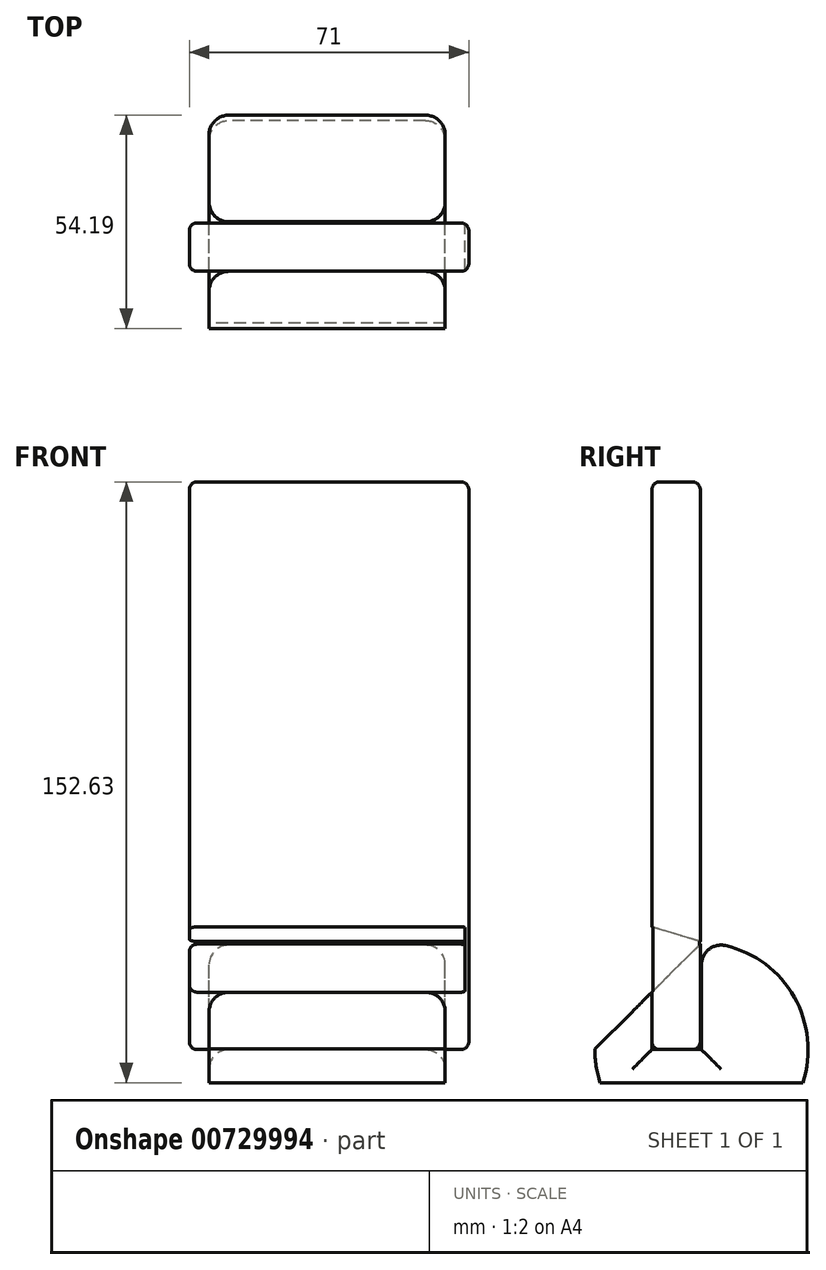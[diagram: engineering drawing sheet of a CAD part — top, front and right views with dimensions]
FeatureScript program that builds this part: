
annotation { "Feature Type Name" : "Feature", "Feature Type Description" : "" }
export const myFeature = defineFeature(function(context is Context, id is Id, definition is map)
    precondition{}
    {
        {
            var Q0;
            Q0=qCreatedBy(makeId("Right.planeOp"),FACE);
            var sketch = newSketch(context, id + "F0", { "sketchPlane" : qUnion([Q0])});
            skLineSegment(sketch, "E0.bottom", {"start": v(0, 0) * mm, "end": v(12.3, 0) * mm});
            skLineSegment(sketch, "E0.top", {"start": v(0, 144.2) * mm, "end": v(12.3, 144.2) * mm});
            skLineSegment(sketch, "E0.left", {"start": v(0, 0) * mm, "end": v(0, 144.2) * mm});
            skLineSegment(sketch, "E0.right", {"start": v(12.3, 0) * mm, "end": v(12.3, 144.2) * mm});
            skSolve(sketch);
        }
        {
            var Q0;
            Q0=makeQuery(id+"F0.imprint","IMPRINT",FACE,{"disambiguationData":[TD([[makeQuery(id+"F0.imprint","IMPRINT",EDGE,{"derivedFrom":sQuery(id+"F0.wireOp",EDGE,"E0.bottom")}),1.0]])]});
            extrude(context, id + "F1", {"entities" : qUnion([Q0]), "depth" : 71 * mm, "offsetDistance" : 25 * mm});
        }
        {
            var Q0;
            Q0=makeQuery(id+"F1.opExtrude","SWEPT_EDGE",EDGE,{"disambiguationData":[OSD([sQuery(id+"F0.wireOp",EDGE,"E0.top"),sQuery(id+"F0.wireOp",EDGE,"E0.right")])]});
            var Q1;
            Q1=makeQuery(id+"F1.opExtrude","CAP_FACE",FACE,{"disambiguationData":[OSD([sQuery(id+"F0.wireOp",EDGE,"E0.bottom"),sQuery(id+"F0.wireOp",EDGE,"E0.top"),sQuery(id+"F0.wireOp",EDGE,"E0.left"),sQuery(id+"F0.wireOp",EDGE,"E0.right")])],"isStart":true});
            var Q2;
            Q2=makeQuery(id+"F1.opExtrude","SWEPT_EDGE",EDGE,{"disambiguationData":[OSD([sQuery(id+"F0.wireOp",EDGE,"E0.bottom"),sQuery(id+"F0.wireOp",EDGE,"E0.right")])]});
            var Q3;
            Q3=makeQuery(id+"F1.opExtrude","CAP_FACE",FACE,{"disambiguationData":[OSD([sQuery(id+"F0.wireOp",EDGE,"E0.bottom"),sQuery(id+"F0.wireOp",EDGE,"E0.top"),sQuery(id+"F0.wireOp",EDGE,"E0.left"),sQuery(id+"F0.wireOp",EDGE,"E0.right")])],"isStart":false});
            var Q4;
            Q4=makeQuery(id+"F1.opExtrude","SWEPT_FACE",FACE,{"disambiguationData":[OSD([sQuery(id+"F0.wireOp",EDGE,"E0.top")])]});
            var Q5;
            Q5=makeQuery(id+"F1.opExtrude","SWEPT_FACE",FACE,{"disambiguationData":[OSD([sQuery(id+"F0.wireOp",EDGE,"E0.left")])]});
            var Q6;
            Q6=makeQuery(id+"F1.opExtrude","SWEPT_FACE",FACE,{"disambiguationData":[OSD([sQuery(id+"F0.wireOp",EDGE,"E0.right")])]});
            var Q7;
            Q7=makeQuery(id+"F1.opExtrude","SWEPT_FACE",FACE,{"disambiguationData":[OSD([sQuery(id+"F0.wireOp",EDGE,"E0.bottom")])]});
            var Q8;
            Q8=makeQuery(id+"F1.opExtrude","SWEPT_EDGE",EDGE,{"disambiguationData":[OSD([sQuery(id+"F0.wireOp",EDGE,"E0.top"),sQuery(id+"F0.wireOp",EDGE,"E0.left")])]});
            var Q9;
            Q9=makeQuery(id+"F1.opExtrude","CAP_EDGE",EDGE,{"disambiguationData":[OSD([sQuery(id+"F0.wireOp",EDGE,"E0.bottom")])],"isStart":true});
            var Q10;
            Q10=makeQuery(id+"F1.opExtrude","CAP_EDGE",EDGE,{"disambiguationData":[OSD([sQuery(id+"F0.wireOp",EDGE,"E0.bottom")])],"isStart":false});
            var Q11;
            Q11=makeQuery(id+"F1.opExtrude","CAP_EDGE",EDGE,{"disambiguationData":[OSD([sQuery(id+"F0.wireOp",EDGE,"E0.top")])],"isStart":true});
            var Q12;
            Q12=makeQuery(id+"F1.opExtrude","CAP_EDGE",EDGE,{"disambiguationData":[OSD([sQuery(id+"F0.wireOp",EDGE,"E0.left")])],"isStart":false});
            var Q13;
            Q13=makeQuery(id+"F1.opExtrude","CAP_EDGE",EDGE,{"disambiguationData":[OSD([sQuery(id+"F0.wireOp",EDGE,"E0.left")])],"isStart":true});
            var Q14;
            Q14=makeQuery(id+"F1.opExtrude","CAP_EDGE",EDGE,{"disambiguationData":[OSD([sQuery(id+"F0.wireOp",EDGE,"E0.right")])],"isStart":false});
            var Q15;
            Q15=makeQuery(id+"F1.opExtrude","CAP_EDGE",EDGE,{"disambiguationData":[OSD([sQuery(id+"F0.wireOp",EDGE,"E0.right")])],"isStart":true});
            var Q16;
            Q16=makeQuery(id+"F1.opExtrude","SWEPT_EDGE",EDGE,{"disambiguationData":[OSD([sQuery(id+"F0.wireOp",EDGE,"E0.bottom"),sQuery(id+"F0.wireOp",EDGE,"E0.left")])]});
            var Q17;
            Q17=makeQuery(id+"F1.opExtrude","CAP_EDGE",EDGE,{"disambiguationData":[OSD([sQuery(id+"F0.wireOp",EDGE,"E0.top")])],"isStart":false});
            fillet(context, id + "F2", {"entities" : qUnion([Q0, Q1, Q2, Q3, Q4, Q5, Q6, Q7, Q8, Q9, Q10, Q11, Q12, Q13, Q14, Q15, Q16, Q17]), "radius" : 2 * mm, "tangentPropagation" : true, "allowEdgeOverflow" : false});
        }
        {
            var Q0;
            Q0=makeQuery(id+"F1.opExtrude","SWEPT_BODY",BODY,{"disambiguationData":[OSD([sQuery(id+"F0.wireOp",EDGE,"E0.bottom"),sQuery(id+"F0.wireOp",EDGE,"E0.top"),sQuery(id+"F0.wireOp",EDGE,"E0.left"),sQuery(id+"F0.wireOp",EDGE,"E0.right")])]});
            var Q1;
            Q1=qCreatedBy(makeId("Origin.pointOp"),VERTEX);
            transform(context, id + "F3", {"entities" : qUnion([Q0]), "transformType" : TransformType.TRANSLATION_3D, "dx" : -35 * mm, "dy" : 0 * mm, "dz" : 0 * mm, "makeCopy" : false});
        }
        {
            var Q0;
            Q0=qCreatedBy(makeId("Right.planeOp"),FACE);
            var sketch = newSketch(context, id + "F4", { "sketchPlane" : qUnion([Q0])});
            skLineSegment(sketch, "E1.bottom", {"start": v(0, 0) * mm, "end": v(12.58, 0) * mm});
            skLineSegment(sketch, "E1.top", {"start": v(0, 49.2) * mm, "end": v(12.58, 49.2) * mm});
            skLineSegment(sketch, "E1.left", {"start": v(0, 0) * mm, "end": v(0, 49.2) * mm});
            skLineSegment(sketch, "E1.right", {"start": v(12.58, 0) * mm, "end": v(12.58, 49.2) * mm});
            skCircle(sketch, "E2", {"center": v(12.58, 0) * mm, "radius": 27.1 * mm});
            skLineSegment(sketch, "E3.bottom", {"start": v(-28.1, 38.83) * mm, "end": v(49.11, 38.83) * mm});
            skLineSegment(sketch, "E3.top", {"start": v(-28.1, -8.43) * mm, "end": v(49.11, -8.43) * mm});
            skLineSegment(sketch, "E3.left", {"start": v(-28.1, 38.83) * mm, "end": v(-28.1, -8.43) * mm});
            skLineSegment(sketch, "E3.right", {"start": v(49.11, 38.83) * mm, "end": v(49.11, -8.43) * mm});
            skSolve(sketch);
        }
        {
            var Q0;
            {var subQ5=sQuery(id+"F4.wireOp",EDGE,"E1.bottom");Q0=makeQuery(id+"F4.imprint","IMPRINT",FACE,{"disambiguationData":[TD([[makeQuery(id+"F4.imprint","IMPRINT",EDGE,{"derivedFrom":subQ5}),-1.0]])]});}
            extrude(context, id + "F5", {"entities" : qUnion([Q0]), "depth" : 60 * mm, "offsetDistance" : 25 * mm});
        }
        {
            var Q0;
            Q0=makeQuery(id+"F5.opExtrude","SWEPT_BODY",BODY,{"disambiguationData":[OSD([sQuery(id+"F4.wireOp",EDGE,"E1.bottom"),sQuery(id+"F4.wireOp",EDGE,"E1.left"),sQuery(id+"F4.wireOp",EDGE,"E1.right"),sQuery(id+"F4.wireOp",EDGE,"E2"),sQuery(id+"F4.wireOp",EDGE,"E3.top")])]});
            transform(context, id + "F6", {"entities" : qUnion([Q0]), "transformType" : TransformType.TRANSLATION_3D, "dx" : -30 * mm, "dy" : 0 * mm, "dz" : 0 * mm, "makeCopy" : false});
        }
        {
            var Q0;
            Q0=qCreatedBy(makeId("Right.planeOp"),FACE);
            var sketch = newSketch(context, id + "F7", { "sketchPlane" : qUnion([Q0])});
            skLineSegment(sketch, "E4", {"start": v(-14.65, 0) * mm, "end": v(12.82, 27.28) * mm});
            skLineSegment(sketch, "E5", {"start": v(12.82, 27.28) * mm, "end": v(-8.53, 33.7) * mm});
            skLineSegment(sketch, "E6", {"start": v(-8.53, 33.7) * mm, "end": v(-30.89, 16.46) * mm});
            skLineSegment(sketch, "E7", {"start": v(-30.89, 16.46) * mm, "end": v(-14.65, 0) * mm});
            skSolve(sketch);
        }
        {
            var Q0;
            Q0=makeQuery(id+"F7.imprint","IMPRINT",FACE,{"disambiguationData":[TD([[makeQuery(id+"F7.imprint","IMPRINT",EDGE,{"derivedFrom":sQuery(id+"F7.wireOp",EDGE,"E4")}),1.0]])]});
            extrude(context, id + "F8", {"entities" : qUnion([Q0]), "operationType" : NewBodyOperationType.REMOVE, "endBound" : BoundingType.SYMMETRIC, "oppositeDirection" : true, "depth" : 70 * mm, "offsetDistance" : 25 * mm});
        }
        {
            var Q0;
            Q0=makeQuery(id+"F5.opExtrude","CAP_EDGE",EDGE,{"disambiguationData":[OSD([sQuery(id+"F4.wireOp",EDGE,"E1.right")])],"isStart":false});
            var Q1;
            Q1=makeQuery(id+"F5.opExtrude","CAP_EDGE",EDGE,{"disambiguationData":[OSD([sQuery(id+"F4.wireOp",EDGE,"E1.bottom")])],"isStart":false});
            var Q2;
            Q2=makeQuery(id+"F5.opExtrude","CAP_EDGE",EDGE,{"disambiguationData":[OSD([sQuery(id+"F4.wireOp",EDGE,"E1.bottom")])],"isStart":true});
            var Q3;
            Q3=makeQuery(id+"F5.opExtrude","CAP_EDGE",EDGE,{"disambiguationData":[OSD([sQuery(id+"F4.wireOp",EDGE,"E1.left")])],"isStart":true});
            var Q4;
            Q4=makeQuery(id+"F5.opExtrude","CAP_EDGE",EDGE,{"disambiguationData":[OSD([sQuery(id+"F4.wireOp",EDGE,"E1.left")])],"isStart":false});
            var Q5;
            Q5=makeQuery(id+"F5.opExtrude","CAP_EDGE",EDGE,{"disambiguationData":[OSD([sQuery(id+"F4.wireOp",EDGE,"E1.right")])],"isStart":true});
            fillet(context, id + "F9", {"entities" : qUnion([Q0, Q1, Q2, Q3, Q4, Q5]), "radius" : 5 * mm, "tangentPropagation" : true, "allowEdgeOverflow" : false});
        }
        {
            var Q0;
            {var subQ0=sQuery(id+"F4.wireOp",EDGE,"E2");var subQ1=sQuery(id+"F4.wireOp",EDGE,"E1.right");Q0=makeQuery(id+"F9.opFillet","BLEND_EDGE",EDGE,{"blendedFrom":[makeQuery(id+"F5.opExtrude","CAP_EDGE",EDGE,{"disambiguationData":[OSD([subQ1])],"isStart":false}),makeQuery(id+"F5.opExtrude","SWEPT_FACE",FACE,{"disambiguationData":[OSD([subQ0]),TDD([makeQuery(id+"F4.imprint","IMPRINT",EDGE,{"disambiguationData":[TD([[makeQuery(id+"F4.imprint","INTERSECT",VERTEX,{"disambiguationData":[OD(1.0)],"derivedFrom":[subQ0,sQuery(id+"F4.wireOp",EDGE,"E3.top")]}),-1.0]])],"derivedFrom":subQ0})])]})],"blendedInto":[makeQuery(id+"F5.opExtrude","SWEPT_FACE",FACE,{"disambiguationData":[OSD([subQ0]),TDD([makeQuery(id+"F4.imprint","IMPRINT",EDGE,{"disambiguationData":[TD([[makeQuery(id+"F4.imprint","INTERSECT",VERTEX,{"disambiguationData":[OD(1.0)],"derivedFrom":[subQ0,sQuery(id+"F4.wireOp",EDGE,"E3.top")]}),-1.0]])],"derivedFrom":subQ0})])]})]});}
            var Q1;
            {var subQ0=sQuery(id+"F4.wireOp",EDGE,"E2");var subQ1=sQuery(id+"F4.wireOp",EDGE,"E1.right");Q1=makeQuery(id+"F9.opFillet","BLEND_EDGE",EDGE,{"blendedFrom":[makeQuery(id+"F5.opExtrude","CAP_EDGE",EDGE,{"disambiguationData":[OSD([subQ1])],"isStart":true}),makeQuery(id+"F5.opExtrude","SWEPT_FACE",FACE,{"disambiguationData":[OSD([subQ0]),TDD([makeQuery(id+"F4.imprint","IMPRINT",EDGE,{"disambiguationData":[TD([[makeQuery(id+"F4.imprint","INTERSECT",VERTEX,{"disambiguationData":[OD(1.0)],"derivedFrom":[subQ0,sQuery(id+"F4.wireOp",EDGE,"E3.top")]}),-1.0]])],"derivedFrom":subQ0})])]})],"blendedInto":[makeQuery(id+"F5.opExtrude","SWEPT_FACE",FACE,{"disambiguationData":[OSD([subQ0]),TDD([makeQuery(id+"F4.imprint","IMPRINT",EDGE,{"disambiguationData":[TD([[makeQuery(id+"F4.imprint","INTERSECT",VERTEX,{"disambiguationData":[OD(1.0)],"derivedFrom":[subQ0,sQuery(id+"F4.wireOp",EDGE,"E3.top")]}),-1.0]])],"derivedFrom":subQ0})])]})]});}
            var Q2;
            {var subQ2=sQuery(id+"F4.wireOp",EDGE,"E1.right");Q2=makeQuery(id+"F9.opFillet","BLEND_EDGE",EDGE,{"blendedFrom":[makeQuery(id+"F5.opExtrude","CAP_EDGE",EDGE,{"disambiguationData":[OSD([subQ2])],"isStart":false}),makeQuery(id+"F8.boolean.opBoolean","COPY",FACE,{"disambiguationData":[TD([makeQuery(id+"F5.opExtrude","SWEPT_FACE",FACE,{"disambiguationData":[OSD([subQ2])]})])],"derivedFrom":makeQuery(id+"F8.opExtrude","SWEPT_FACE",FACE,{"disambiguationData":[OSD([sQuery(id+"F7.wireOp",EDGE,"E4")])]})})],"blendedInto":[makeQuery(id+"F8.boolean.opBoolean","COPY",FACE,{"disambiguationData":[TD([makeQuery(id+"F5.opExtrude","SWEPT_FACE",FACE,{"disambiguationData":[OSD([subQ2])]})])],"derivedFrom":makeQuery(id+"F8.opExtrude","SWEPT_FACE",FACE,{"disambiguationData":[OSD([sQuery(id+"F7.wireOp",EDGE,"E4")])]})})]});}
            var Q3;
            {var subQ0=sQuery(id+"F4.wireOp",EDGE,"E2");Q3=makeQuery(id+"F8.boolean.opBoolean","INTERSECT",EDGE,{"derivedFrom":[makeQuery(id+"F5.opExtrude","SWEPT_FACE",FACE,{"disambiguationData":[OSD([subQ0]),TDD([makeQuery(id+"F4.imprint","IMPRINT",EDGE,{"disambiguationData":[TD([[makeQuery(id+"F4.imprint","INTERSECT",VERTEX,{"disambiguationData":[OD(1.0)],"derivedFrom":[subQ0,sQuery(id+"F4.wireOp",EDGE,"E3.top")]}),-1.0]])],"derivedFrom":subQ0})])]}),makeQuery(id+"F8.opExtrude","SWEPT_FACE",FACE,{"disambiguationData":[OSD([sQuery(id+"F7.wireOp",EDGE,"E4")])]})]});}
            var Q4;
            Q4=makeQuery(id+"F8.boolean.opBoolean","INTERSECT",EDGE,{"derivedFrom":[makeQuery(id+"F5.opExtrude","SWEPT_FACE",FACE,{"disambiguationData":[OSD([sQuery(id+"F4.wireOp",EDGE,"E1.right")])]}),makeQuery(id+"F8.opExtrude","SWEPT_FACE",FACE,{"disambiguationData":[OSD([sQuery(id+"F7.wireOp",EDGE,"E4")])]})]});
            var Q5;
            {var subQ2=sQuery(id+"F4.wireOp",EDGE,"E1.right");Q5=makeQuery(id+"F9.opFillet","BLEND_EDGE",EDGE,{"blendedFrom":[makeQuery(id+"F5.opExtrude","CAP_EDGE",EDGE,{"disambiguationData":[OSD([subQ2])],"isStart":true}),makeQuery(id+"F8.boolean.opBoolean","COPY",FACE,{"disambiguationData":[TD([makeQuery(id+"F5.opExtrude","SWEPT_FACE",FACE,{"disambiguationData":[OSD([subQ2])]})])],"derivedFrom":makeQuery(id+"F8.opExtrude","SWEPT_FACE",FACE,{"disambiguationData":[OSD([sQuery(id+"F7.wireOp",EDGE,"E4")])]})})],"blendedInto":[makeQuery(id+"F8.boolean.opBoolean","COPY",FACE,{"disambiguationData":[TD([makeQuery(id+"F5.opExtrude","SWEPT_FACE",FACE,{"disambiguationData":[OSD([subQ2])]})])],"derivedFrom":makeQuery(id+"F8.opExtrude","SWEPT_FACE",FACE,{"disambiguationData":[OSD([sQuery(id+"F7.wireOp",EDGE,"E4")])]})})]});}
            fillet(context, id + "F10", {"entities" : qUnion([Q0, Q1, Q2, Q3, Q4, Q5]), "radius" : 5 * mm, "tangentPropagation" : true, "allowEdgeOverflow" : false});
        }
    });
